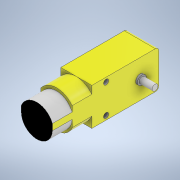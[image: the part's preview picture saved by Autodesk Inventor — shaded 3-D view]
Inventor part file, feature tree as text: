
AUTODESK INVENTOR PART (.ipt)
format: ipt  version: 2020 (Build 240168000, 168)  size: 207,872 bytes
history: native  units: mm
features: extrude x8, sketch x8, other x2, fillet x2, mirror x1
ambient origin geometry x8: Origin, YZ Plane, XZ Plane, XY Plane, X Axis, Y Axis, Z Axis, Center Point
bodies: Body1 (feature_tree)
feature tree (21):
  other  "Sólido1"
  extrude  "Extrusão1"  Depth=22.5mm
  extrude  "Extrusão2"  Depth=64.2mm
  extrude  "Extrusão3"  Depth=1.1mm
  other  "Plano de trabalho1"
  mirror  "Espelhamento1"
  fillet  "Arredondamento1"  Radius=1.1mm
  fillet  "Arredondamento2"  Radius=3.6mm
  extrude  "Extrusão4"  [1 undecoded]
  extrude  "Extrusão5"  Depth=2.0mm
  extrude  "Extrusão6"  Depth=2.5mm
  extrude  "Extrusão7"  Depth=17.5mm
  extrude  "Extrusão8"  TaperAngle=0.0deg  [1 undecoded]
  sketch  "Esboço1"  dims[d0=18.8mm d1=22.5mm]
  sketch  "Esboço2"  dims[d2=64.2mm d3=0.0mm d4=11.25mm]
  sketch  "Esboço3"  dims[d5=11.2mm d6=5.4mm d7=1.1mm d8=0.0mm d9=3.6mm]
  sketch  "Esboço4"  dims[d10=7.9mm d11=0.0mm d12=-9.4mm]
  sketch  "Esboço5"  dims[d13=2.0mm d14=2.0mm]
  sketch  "Esboço6"  dims[d15=31.8mm d16=2.5mm]
  sketch  "Esboço7"  dims[d17=3.0mm d18=17.5mm]
  sketch  "Esboço9"  dims[d19=3.0mm d20=0.0mm d21=0.0mm d22=23.8mm d23=0.0mm d24=23.8mm d25=0.0mm d26=11.9mm d27=0.0mm d29=11.9mm d30=0.0mm]
note: 2 required parameter values undecoded (feature->parameter linkage not recoverable at this tier; creation-order binding heuristic only, values carry confidence <= 0.55)
